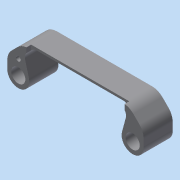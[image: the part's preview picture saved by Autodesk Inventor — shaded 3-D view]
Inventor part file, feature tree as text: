
AUTODESK INVENTOR PART (.ipt)
format: ipt  version: 2016 (Build 200138000, 138)  size: 176,640 bytes
history: native  units: in
note: dims shown in document units (in); Inventor stores cm internally (conversion verified against a paired STEP export)
features: extrude x3, sketch x3, projected_geometry x2
ambient origin geometry x8: Origin, YZ Plane, XZ Plane, XY Plane, X Axis, Y Axis, Z Axis, Center Point
bodies: Body1 (feature_tree)
feature tree (8):
  extrude  "Extrusion2"  Depth=0.125in
  extrude  "Extrusion3"  Depth=0.125in
  extrude  "Extrusion4"  Depth=0.095in
  sketch  "Sketch1"  dims[d7=0.125in d8=0.125in]
  sketch  "Sketch4"  dims[d9=0.125in d10=0.125in]
  projected_geometry  "Projected Loop1"
  sketch  "Sketch5"  dims[d11=0.237in d12=0.095in d13=0.063in d14=0.02in d15=75.0deg d16=0.984in d19=0.122in d20=0.122in d21=0.21in d22=0.0in d24=0.07in d25=0.07in d26=0.04in d27=0.0in d28=0.12in d29=0.041in d30=0.05in d31=0.0in]
  projected_geometry  "Projected Loop2"
